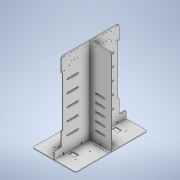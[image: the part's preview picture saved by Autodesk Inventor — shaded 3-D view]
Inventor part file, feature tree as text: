
AUTODESK INVENTOR PART (.ipt)
format: ipt  version: 2022 (Build 260153000, 153)  size: 1,126,400 bytes
history: native  units: mm
features: sketch x16, extrude x15, projected_geometry x7, other x6
ambient origin geometry x8: Origin, YZ Plane, XZ Plane, XY Plane, X Axis, Y Axis, Z Axis, Center Point
bodies: Body1 (feature_tree), Body2 (feature_tree), Body3 (feature_tree)
feature tree (44):
  other  "Твердое тело1"
  extrude  "Выдавливание1"  Depth=300.0mm
  other  "РабПлоскость1"
  extrude  "Выдавливание2"  Depth=500.0mm
  other  "РабПлоскость2"
  extrude  "Выдавливание3"  Depth=256.666667mm
  sketch  "Эскиз5"
  extrude  "Выдавливание4"  Depth=243.333333mm
  extrude  "Выдавливание5"  Depth=4.0mm
  extrude  "Выдавливание6"  Depth=4.0mm
  extrude  "Выдавливание7"  Depth=4.0mm
  sketch  "Эскиз9"
  extrude  "Выдавливание11"  Depth=4.0mm
  extrude  "Выдавливание13"  Depth=6.0mm
  sketch  "Эскиз16"
  sketch  "Эскиз17"
  extrude  "Выдавливание14"  Depth=30.0mm
  extrude  "Выдавливание15"  Depth=6.0mm
  other  "РабПлоскость3"
  extrude  "Выдавливание16"  Depth=6.0mm
  sketch  "Эскиз19"
  extrude  "Выдавливание17"  Depth=6.0mm
  extrude  "Выдавливание18"  Depth=6.0mm
  extrude  "Выдавливание19"  Depth=6.0mm
  sketch  "Эскиз1"
  sketch  "Эскиз2"
  sketch  "Эскиз4"
  other  "Твердое тело2"
  other  "Твердое тело3"
  projected_geometry  "Спроецированная петля1"
  sketch  "Эскиз6"
  projected_geometry  "Спроецированная петля2"
  sketch  "Эскиз7"
  projected_geometry  "Спроецированная петля3"
  projected_geometry  "Спроецированная петля4"
  sketch  "Эскиз13"
  projected_geometry  "Спроецированная петля5"
  sketch  "Эскиз15"
  projected_geometry  "Спроецированная петля6"
  sketch  "Эскиз18"
  sketch  "Эскиз20"
  sketch  "Эскиз21"
  sketch  "Эскиз22"
  projected_geometry  "Спроецированная петля7"
